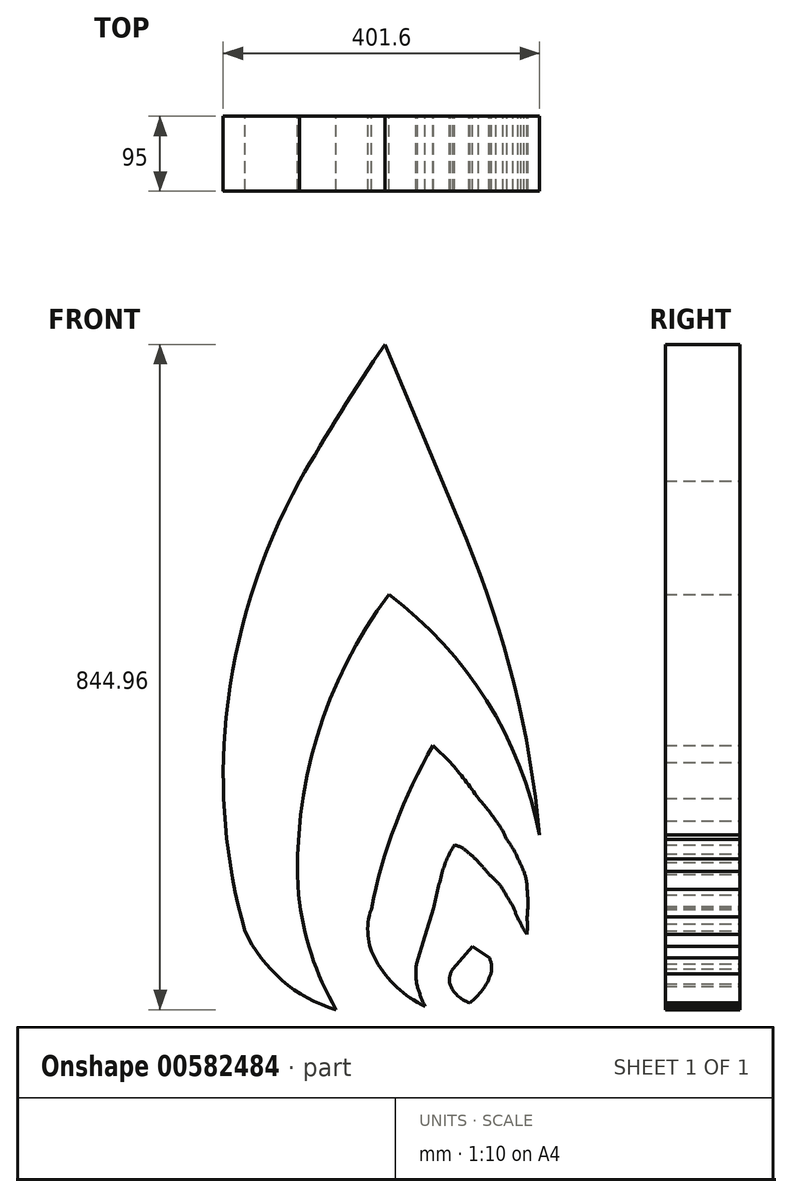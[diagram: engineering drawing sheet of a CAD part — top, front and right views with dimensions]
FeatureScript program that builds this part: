
annotation { "Feature Type Name" : "Feature", "Feature Type Description" : "" }
export const myFeature = defineFeature(function(context is Context, id is Id, definition is map)
    precondition{}
    {
        {
            var Q0;
            Q0=qCreatedBy(makeId("Front.planeOp"),FACE);
            var sketch = newSketch(context, id + "F0", { "sketchPlane" : qUnion([Q0])});
            skArc(sketch, "E0", {"start": v(-32.79, 22) * mm, "mid": v(-36.43, 12.86) * mm, "end": v(-36.36, 3.02) * mm});
            skArc(sketch, "E1", {"start": v(-36.36, 3.02) * mm, "mid": v(-26.64, -11.96) * mm, "end": v(-11.2, -20.9) * mm});
            skArc(sketch, "E2", {"start": v(-11.2, -20.9) * mm, "mid": v(5.06, -4.62) * mm, "end": v(15.6, 15.83) * mm});
            skLineSegment(sketch, "E3", {"start": v(-32.79, 22) * mm, "end": v(-7.6, 50.86) * mm});
            skLineSegment(sketch, "E4", {"start": v(-7.6, 50.86) * mm, "end": v(13.66, 35.89) * mm});
            skArc(sketch, "E5", {"start": v(15.6, 15.83) * mm, "mid": v(16.56, 26.05) * mm, "end": v(13.66, 35.89) * mm});
            skPoint(sketch, "E6", {"position": v(-68.12, -25.36) * mm});
            skPoint(sketch, "E7", {"position": v(-77.87, 0) * mm});
            skPoint(sketch, "E8", {"position": v(-78.75, 28.7) * mm});
            skPoint(sketch, "E9", {"position": v(-68.12, 64.14) * mm});
            skPoint(sketch, "E10", {"position": v(-57.48, 98.7) * mm});
            skPoint(sketch, "E11", {"position": v(-46.25, 144.2) * mm});
            skPoint(sketch, "E12", {"position": v(-30.84, 179.4) * mm});
            skPoint(sketch, "E13", {"position": v(-12.13, 168.4) * mm});
            skPoint(sketch, "E14", {"position": v(0, 157.4) * mm});
            skPoint(sketch, "E15", {"position": v(13.19, 142) * mm});
            skPoint(sketch, "E16", {"position": v(30.8, 123.3) * mm});
            skPoint(sketch, "E17", {"position": v(44, 101.3) * mm});
            skPoint(sketch, "E18", {"position": v(53.91, 79.3) * mm});
            skPoint(sketch, "E19", {"position": v(61.62, 66.09) * mm});
            skPoint(sketch, "E20", {"position": v(61.62, 88.1) * mm});
            skPoint(sketch, "E21", {"position": v(61.62, 123.3) * mm});
            skPoint(sketch, "E22", {"position": v(57.61, 145.62) * mm});
            skPoint(sketch, "E23", {"position": v(50.41, 161.68) * mm});
            skPoint(sketch, "E24", {"position": v(35.8, 186.39) * mm});
            skPoint(sketch, "E25", {"position": v(22.25, 209.93) * mm});
            skPoint(sketch, "E26", {"position": v(0, 238.47) * mm});
            skPoint(sketch, "E27", {"position": v(-35.79, 284.59) * mm});
            skArc(sketch, "E28", {"start": v(0, 238.47) * mm, "mid": v(-17.32, 261.97) * mm, "end": v(-35.79, 284.59) * mm});
            skArc(sketch, "E29", {"start": v(22.25, 209.93) * mm, "mid": v(11.57, 224.55) * mm, "end": v(0, 238.47) * mm});
            skArc(sketch, "E30", {"start": v(35.8, 186.39) * mm, "mid": v(29.9, 198.66) * mm, "end": v(22.25, 209.93) * mm});
            skArc(sketch, "E31", {"start": v(57.61, 145.62) * mm, "mid": v(54.06, 153.67) * mm, "end": v(50.41, 161.68) * mm});
            skArc(sketch, "E32", {"start": v(50.41, 161.68) * mm, "mid": v(43.92, 174.5) * mm, "end": v(35.8, 186.39) * mm});
            skArc(sketch, "E33", {"start": v(61.62, 123.3) * mm, "mid": v(60.69, 134.65) * mm, "end": v(57.61, 145.62) * mm});
            skArc(sketch, "E34", {"start": v(61.62, 88.1) * mm, "mid": v(62.7, 105.7) * mm, "end": v(61.62, 123.3) * mm});
            skArc(sketch, "E35", {"start": v(61.62, 66.09) * mm, "mid": v(61.94, 77.1) * mm, "end": v(61.62, 88.1) * mm});
            skArc(sketch, "E36", {"start": v(53.91, 79.3) * mm, "mid": v(57.3, 72.41) * mm, "end": v(61.62, 66.09) * mm});
            skArc(sketch, "E37", {"start": v(44, 101.3) * mm, "mid": v(48.4, 90.04) * mm, "end": v(53.91, 79.3) * mm});
            skArc(sketch, "E38", {"start": v(30.8, 123.3) * mm, "mid": v(37.2, 112.18) * mm, "end": v(44, 101.3) * mm});
            skArc(sketch, "E39", {"start": v(30.8, 123.3) * mm, "mid": v(22.72, 133.34) * mm, "end": v(13.19, 142) * mm});
            skArc(sketch, "E40", {"start": v(13.19, 142) * mm, "mid": v(6.96, 150.02) * mm, "end": v(0, 157.4) * mm});
            skArc(sketch, "E41", {"start": v(0, 157.4) * mm, "mid": v(-5.66, 163.35) * mm, "end": v(-12.13, 168.4) * mm});
            skArc(sketch, "E42", {"start": v(-12.13, 168.4) * mm, "mid": v(-20.52, 175.55) * mm, "end": v(-30.84, 179.4) * mm});
            skArc(sketch, "E43", {"start": v(-30.84, 179.4) * mm, "mid": v(-39.87, 162.38) * mm, "end": v(-46.25, 144.2) * mm});
            skArc(sketch, "E44", {"start": v(-46.25, 144.2) * mm, "mid": v(-52.16, 121.52) * mm, "end": v(-57.48, 98.7) * mm});
            skLineSegment(sketch, "E45", {"start": v(-57.48, 98.7) * mm, "end": v(-68.12, 64.14) * mm});
            skLineSegment(sketch, "E46", {"start": v(-68.12, 64.14) * mm, "end": v(-78.75, 28.7) * mm});
            skArc(sketch, "E47", {"start": v(-78.75, 28.7) * mm, "mid": v(-79.65, 14.3) * mm, "end": v(-77.87, 0) * mm});
            skArc(sketch, "E48", {"start": v(-77.87, 0) * mm, "mid": v(-73.48, -12.87) * mm, "end": v(-68.12, -25.36) * mm});
            skPoint(sketch, "E49", {"position": v(-57.87, 305.8) * mm});
            skPoint(sketch, "E50", {"position": v(-115.1, 37.28) * mm});
            skLineSegment(sketch, "E51", {"start": v(-35.79, 284.59) * mm, "end": v(-57.87, 305.8) * mm});
            skArc(sketch, "E52", {"start": v(-130.4, 32.58) * mm, "mid": v(-103.65, -1.1) * mm, "end": v(-68.12, -25.36) * mm});
            skArc(sketch, "E53", {"start": v(-57.87, 305.8) * mm, "mid": v(-105.63, 205.1) * mm, "end": v(-136.25, 97.92) * mm});
            skArc(sketch, "E54", {"start": v(-136.25, 97.92) * mm, "mid": v(-140.42, 64.62) * mm, "end": v(-130.4, 32.58) * mm});
            skArc(sketch, "E55", {"start": v(-228.8, 115.94) * mm, "mid": v(-212.46, 40.6) * mm, "end": v(-180.9, -29.73) * mm});
            skArc(sketch, "E56", {"start": v(-227.26, 205.29) * mm, "mid": v(-229.9, 160.64) * mm, "end": v(-228.8, 115.94) * mm});
            skArc(sketch, "E57", {"start": v(-113.88, 497.52) * mm, "mid": v(-205.36, 316.97) * mm, "end": v(-228.8, 115.94) * mm});
            skArc(sketch, "E58", {"start": v(77.33, 192.23) * mm, "mid": v(10.3, 362.78) * mm, "end": v(-113.88, 497.52) * mm});
            skLineSegment(sketch, "E59", {"start": v(-119.1, 815.23) * mm, "end": v(-16.2, 569.32) * mm});
            skArc(sketch, "E60", {"start": v(77.33, 192.23) * mm, "mid": v(45.04, 384.36) * mm, "end": v(-16.2, 569.32) * mm});
            skArc(sketch, "E61", {"start": v(-296.73, 70.04) * mm, "mid": v(-249.61, 7.62) * mm, "end": v(-180.9, -29.73) * mm});
            skArc(sketch, "E62", {"start": v(-320.5, 341.57) * mm, "mid": v(-321.51, 204.68) * mm, "end": v(-296.73, 70.04) * mm});
            skArc(sketch, "E63", {"start": v(-227.26, 641.98) * mm, "mid": v(-288.98, 496.47) * mm, "end": v(-320.5, 341.57) * mm});
            skArc(sketch, "E64", {"start": v(-119.1, 815.23) * mm, "mid": v(-174.88, 729.67) * mm, "end": v(-227.26, 641.98) * mm});
            skSolve(sketch);
        }
        {
            var Q0;
            Q0 = qSketchRegion(id + "F0", true);
            extrude(context, id + "F1", {"entities" : qUnion([Q0]), "depth" : 95 * mm, "offsetDistance" : 25 * mm});
        }
    });
